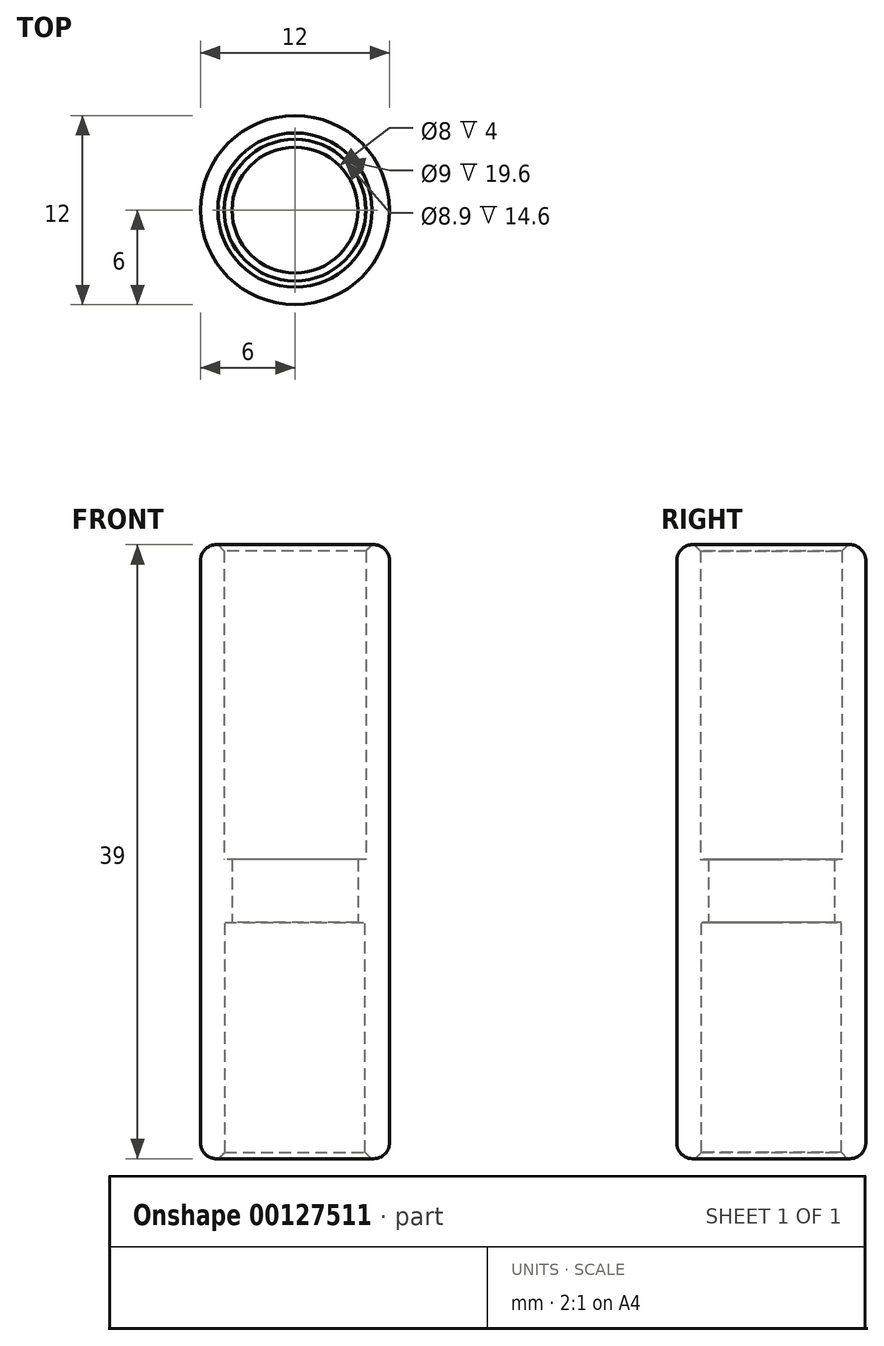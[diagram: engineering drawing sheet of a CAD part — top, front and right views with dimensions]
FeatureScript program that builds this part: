
annotation { "Feature Type Name" : "Feature", "Feature Type Description" : "" }
export const myFeature = defineFeature(function(context is Context, id is Id, definition is map)
    precondition{}
    {
        {
            var Q0;
            Q0=qCreatedBy(makeId("Top.planeOp"),FACE);
            var sketch = newSketch(context, id + "F0", { "sketchPlane" : qUnion([Q0])});
            skCircle(sketch, "E0", {"center": v(0, 0) * mm, "radius": 4 * mm});
            skCircle(sketch, "E1", {"center": v(0, 0) * mm, "radius": 6 * mm});
            skSolve(sketch);
        }
        {
            var Q0;
            Q0=qSketchRegion(id+"F0",true);
            extrude(context, id + "F1", {"entities" : qUnion([Q0]), "depth" : 4 * mm});
        }
        {
            var Q0;
            Q0 = qSketchRegion(id + "F0", true);
            extrude(context, id + "F2", {"entities" : qUnion([Q0]), "operationType" : NewBodyOperationType.ADD, "depth" : 4 * mm});
        }
        {
            var Q0;
            Q0=makeQuery(id+"F1.opExtrude","CAP_FACE",FACE,{"disambiguationData":[OSD([sQuery(id+"F0.wireOp",EDGE,"E0"),sQuery(id+"F0.wireOp",EDGE,"E1")])],"isStart":false});
            var sketch = newSketch(context, id + "F3", { "sketchPlane" : qUnion([Q0])});
            skCircle(sketch, "E2", {"center": v(0, 0) * mm, "radius": 4.5 * mm});
            skSolve(sketch);
        }
        {
            var Q0;
            Q0=makeQuery(id+"F3.imprint","IMPRINT",FACE,{"disambiguationData":[TD([[makeQuery(id+"F3.imprint","IMPRINT",EDGE,{"derivedFrom":sQuery(id+"F3.wireOp",EDGE,"E2")}),-1.0]])]});
            extrude(context, id + "F4", {"entities" : qUnion([Q0]), "operationType" : NewBodyOperationType.ADD, "depth" : 20 * mm});
        }
        {
            var Q0;
            Q0=makeQuery(id+"F1.opExtrude","CAP_FACE",FACE,{"disambiguationData":[OSD([sQuery(id+"F0.wireOp",EDGE,"E0"),sQuery(id+"F0.wireOp",EDGE,"E1")])],"isStart":true});
            var sketch = newSketch(context, id + "F5", { "sketchPlane" : qUnion([Q0])});
            skCircle(sketch, "E3", {"center": v(0, 0) * mm, "radius": 4.45 * mm});
            skSolve(sketch);
        }
        {
            var Q0;
            Q0=makeQuery(id+"F5.imprint","IMPRINT",FACE,{"disambiguationData":[TD([[makeQuery(id+"F5.imprint","IMPRINT",EDGE,{"derivedFrom":sQuery(id+"F5.wireOp",EDGE,"E3")}),-1.0]])]});
            extrude(context, id + "F6", {"entities" : qUnion([Q0]), "operationType" : NewBodyOperationType.ADD, "depth" : 15 * mm});
        }
        {
            var Q0;
            Q0=makeQuery(id+"F6.opExtrude","CAP_EDGE",EDGE,{"disambiguationData":[OSD([sQuery(id+"F5.wireOp",EDGE,"E3")])],"isStart":false});
            var Q1;
            Q1=makeQuery(id+"F4.opExtrude","CAP_EDGE",EDGE,{"disambiguationData":[OSD([sQuery(id+"F3.wireOp",EDGE,"E2")])],"isStart":false});
            chamfer(context, id + "F7", {"entities" : qUnion([Q0, Q1]), "width" : 0.4 * mm, "tangentPropagation" : true});
        }
        {
            var Q0;
            Q0=makeQuery(id+"F4.opExtrude","CAP_EDGE",EDGE,{"disambiguationData":[OSD([sQuery(id+"F0.wireOp",EDGE,"E1")])],"isStart":false});
            var Q1;
            Q1=makeQuery(id+"F6.opExtrude","CAP_EDGE",EDGE,{"disambiguationData":[OSD([sQuery(id+"F0.wireOp",EDGE,"E1")])],"isStart":false});
            fillet(context, id + "F8", {"entities" : qUnion([Q0, Q1]), "radius" : 1 * mm, "tangentPropagation" : true, "allowEdgeOverflow" : false});
        }
    });
